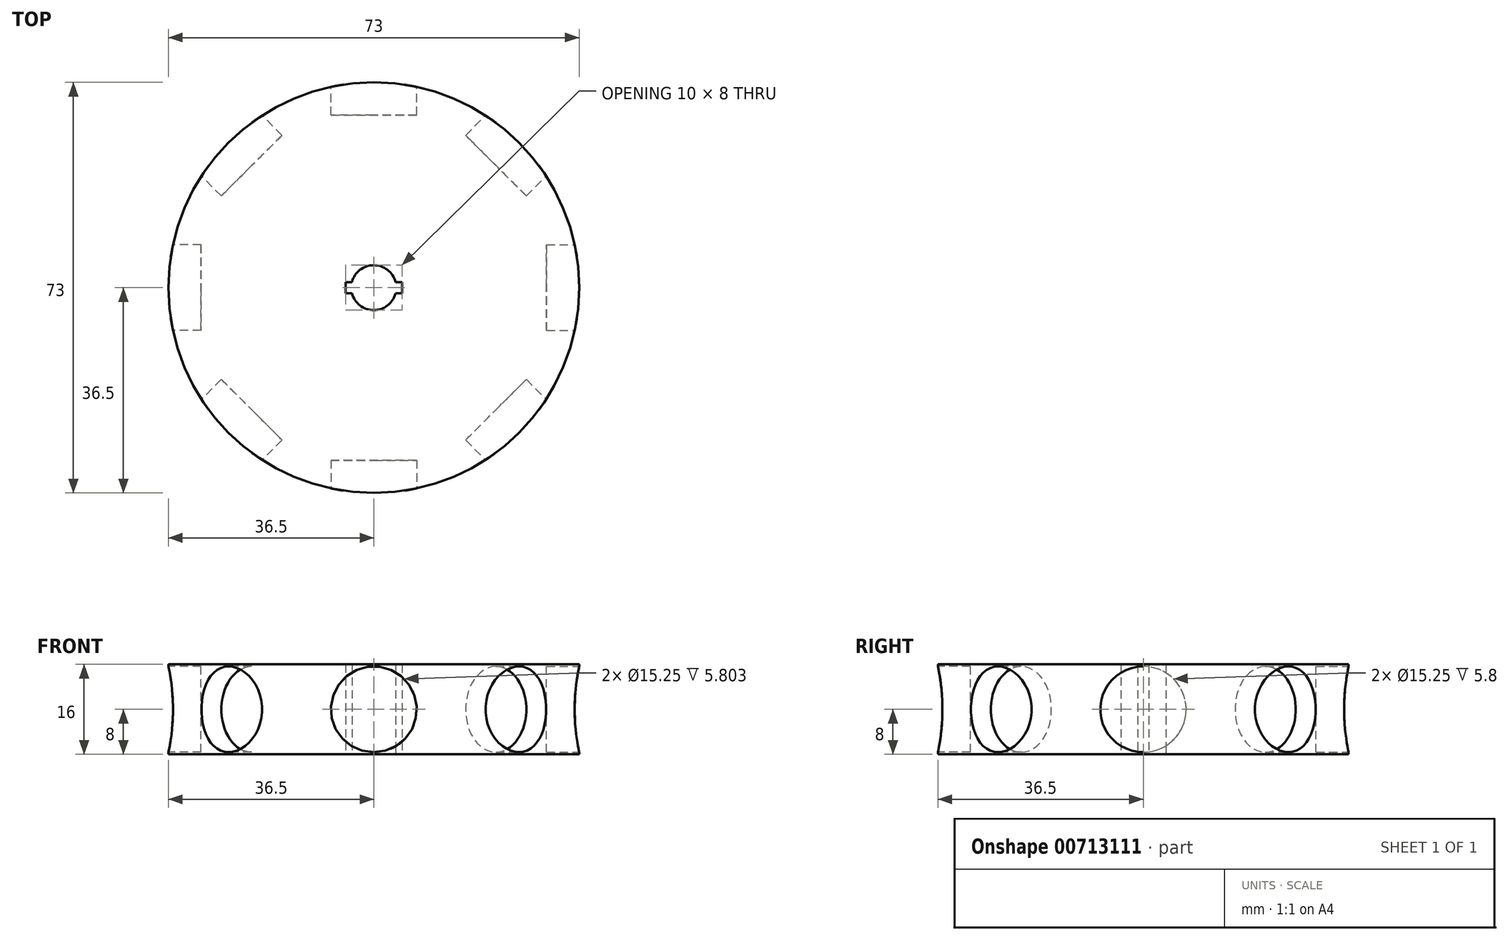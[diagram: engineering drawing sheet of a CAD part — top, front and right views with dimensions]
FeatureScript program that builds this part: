
annotation { "Feature Type Name" : "Feature", "Feature Type Description" : "" }
export const myFeature = defineFeature(function(context is Context, id is Id, definition is map)
    precondition{}
    {
        {
            var Q0;
            Q0=qCreatedBy(makeId("Top.planeOp"),FACE);
            var sketch = newSketch(context, id + "F0", { "sketchPlane" : qUnion([Q0])});
            skCircle(sketch, "E0", {"center": v(0, 0) * mm, "radius": 36.5 * mm});
            skCircle(sketch, "E1", {"center": v(0, 0) * mm, "radius": 4 * mm});
            skLineSegment(sketch, "E2.bottom", {"start": v(-5, 1) * mm, "end": v(5, 1) * mm});
            skLineSegment(sketch, "E2.top", {"start": v(-5, -1) * mm, "end": v(5, -1) * mm});
            skLineSegment(sketch, "E2.left", {"start": v(-5, 1) * mm, "end": v(-5, -1) * mm});
            skLineSegment(sketch, "E2.right", {"start": v(5, 1) * mm, "end": v(5, -1) * mm});
            skSolve(sketch);
        }
        {
            var Q0;
            Q0=makeQuery(id+"F0.imprint","IMPRINT",FACE,{"disambiguationData":[TD([[makeQuery(id+"F0.imprint","IMPRINT",EDGE,{"derivedFrom":sQuery(id+"F0.wireOp",EDGE,"E0")}),1.0]])]});
            extrude(context, id + "F1", {"entities" : qUnion([Q0]), "depth" : 16 * mm, "offsetDistance" : 25 * mm});
        }
        {
            var Q0;
            Q0=qCreatedBy(makeId("Front.planeOp"),FACE);
            cPlane(context, id + "F2", {"entities" : qUnion([Q0]), "cplaneType" : CPlaneType.OFFSET, "offset" : 37 * mm, "width" : 150 * mm, "height" : 150 * mm});
        }
        {
            var Q0;
            Q0=qCreatedBy(id+"F2.planeOp",FACE);
            var sketch = newSketch(context, id + "F3", { "sketchPlane" : qUnion([Q0])});
            skLineSegment(sketch, "E3", {"start": v(0, 0) * mm, "end": v(0, 8) * mm});
            skCircle(sketch, "E4", {"center": v(0, 8) * mm, "radius": 7.62 * mm});
            skSolve(sketch);
        }
        {
            var Q0;
            Q0=qCreatedBy(makeId("Front.planeOp"),FACE);
            var sketch = newSketch(context, id + "F4", { "sketchPlane" : qUnion([Q0])});
            skLineSegment(sketch, "E5", {"start": v(0, 0) * mm, "end": v(0, 16) * mm});
            skSolve(sketch);
        }
        {
            var Q0;
            Q0=makeQuery(id+"F3.imprint","IMPRINT",FACE,{"disambiguationData":[TD([[makeQuery(id+"F3.imprint","IMPRINT",EDGE,{"derivedFrom":sQuery(id+"F3.wireOp",EDGE,"E4")}),1.0]])]});
            extrude(context, id + "F5", {"entities" : qUnion([Q0]), "oppositeDirection" : true, "depth" : 6.3 * mm, "offsetDistance" : 25 * mm, "hasSecondDirection" : true, "secondDirectionOppositeDirection" : false, "secondDirectionDepth" : 2 * mm});
        }
        {
            var Q0;
            Q0=makeQuery(id+"F5.opExtrude","SWEPT_BODY",BODY,{"disambiguationData":[OSD([sQuery(id+"F3.wireOp",EDGE,"E4")])]});
            var Q1;
            Q1=sQuery(id+"F4.wireOp",EDGE,"E5");
            circularPattern(context, id + "F6", {"entities" : qUnion([Q0]), "axis" : qUnion([Q1]), "angle" : 360 * degree, "instanceCount" : 8, "equalSpace" : true});
        }
        {
            var Q0;
            Q0=makeQuery(id+"F5.opExtrude","SWEPT_BODY",BODY,{"disambiguationData":[OSD([sQuery(id+"F3.wireOp",EDGE,"E4")])]});
            var Q1;
            Q1=makeQuery(id+"F6.opPattern","COPY",BODY,{"derivedFrom":makeQuery(id+"F5.opExtrude","SWEPT_BODY",BODY,{"disambiguationData":[OSD([sQuery(id+"F3.wireOp",EDGE,"E4")])]}),"instanceName":"1"});
            var Q2;
            Q2=makeQuery(id+"F6.opPattern","COPY",BODY,{"derivedFrom":makeQuery(id+"F5.opExtrude","SWEPT_BODY",BODY,{"disambiguationData":[OSD([sQuery(id+"F3.wireOp",EDGE,"E4")])]}),"instanceName":"2"});
            var Q3;
            Q3=makeQuery(id+"F6.opPattern","COPY",BODY,{"derivedFrom":makeQuery(id+"F5.opExtrude","SWEPT_BODY",BODY,{"disambiguationData":[OSD([sQuery(id+"F3.wireOp",EDGE,"E4")])]}),"instanceName":"3"});
            var Q4;
            Q4=makeQuery(id+"F6.opPattern","COPY",BODY,{"derivedFrom":makeQuery(id+"F5.opExtrude","SWEPT_BODY",BODY,{"disambiguationData":[OSD([sQuery(id+"F3.wireOp",EDGE,"E4")])]}),"instanceName":"4"});
            var Q5;
            Q5=makeQuery(id+"F6.opPattern","COPY",BODY,{"derivedFrom":makeQuery(id+"F5.opExtrude","SWEPT_BODY",BODY,{"disambiguationData":[OSD([sQuery(id+"F3.wireOp",EDGE,"E4")])]}),"instanceName":"5"});
            var Q6;
            Q6=makeQuery(id+"F6.opPattern","COPY",BODY,{"derivedFrom":makeQuery(id+"F5.opExtrude","SWEPT_BODY",BODY,{"disambiguationData":[OSD([sQuery(id+"F3.wireOp",EDGE,"E4")])]}),"instanceName":"6"});
            var Q7;
            Q7=makeQuery(id+"F6.opPattern","COPY",BODY,{"derivedFrom":makeQuery(id+"F5.opExtrude","SWEPT_BODY",BODY,{"disambiguationData":[OSD([sQuery(id+"F3.wireOp",EDGE,"E4")])]}),"instanceName":"7"});
            var Q8;
            Q8=makeQuery(id+"F1.opExtrude","SWEPT_BODY",BODY,{"disambiguationData":[OSD([sQuery(id+"F0.wireOp",EDGE,"E0")])]});
            booleanBodies(context, id + "F7", {"operationType" : BooleanOperationType.SUBTRACTION, "tools" : qUnion([Q0, Q1, Q2, Q3, Q4, Q5, Q6, Q7]), "targets" : qUnion([Q8])});
        }
    });
